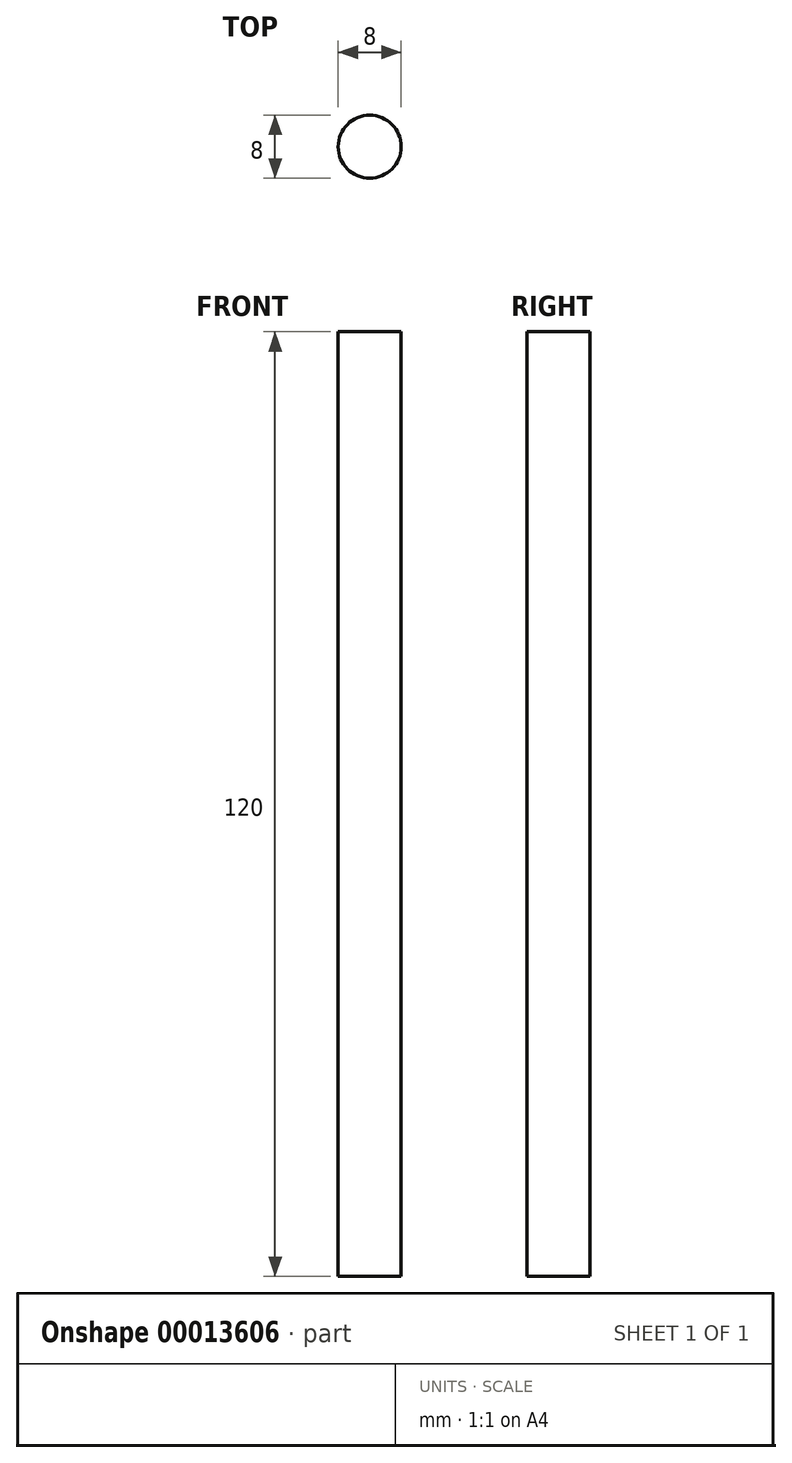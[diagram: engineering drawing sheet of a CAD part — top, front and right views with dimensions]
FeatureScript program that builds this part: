
annotation { "Feature Type Name" : "Feature", "Feature Type Description" : "" }
export const myFeature = defineFeature(function(context is Context, id is Id, definition is map)
    precondition{}
    {
        {
            var Q0;
            Q0=qCreatedBy(makeId("Top.planeOp"),FACE);
            var sketch = newSketch(context, id + "F0", { "sketchPlane" : qUnion([Q0])});
            skCircle(sketch, "E0", {"center": v(0, 0) * mm, "radius": 4 * mm});
            skSolve(sketch);
        }
        {
            var Q0;
            Q0=makeQuery(id+"F0.imprint","IMPRINT",FACE,{"disambiguationData":[TD([[makeQuery(id+"F0.imprint","IMPRINT",EDGE,{"derivedFrom":sQuery(id+"F0.wireOp",EDGE,"E0")}),1.0]])]});
            extrude(context, id + "F1", {"entities" : qUnion([Q0]), "depth" : 120 * mm});
        }
    });
